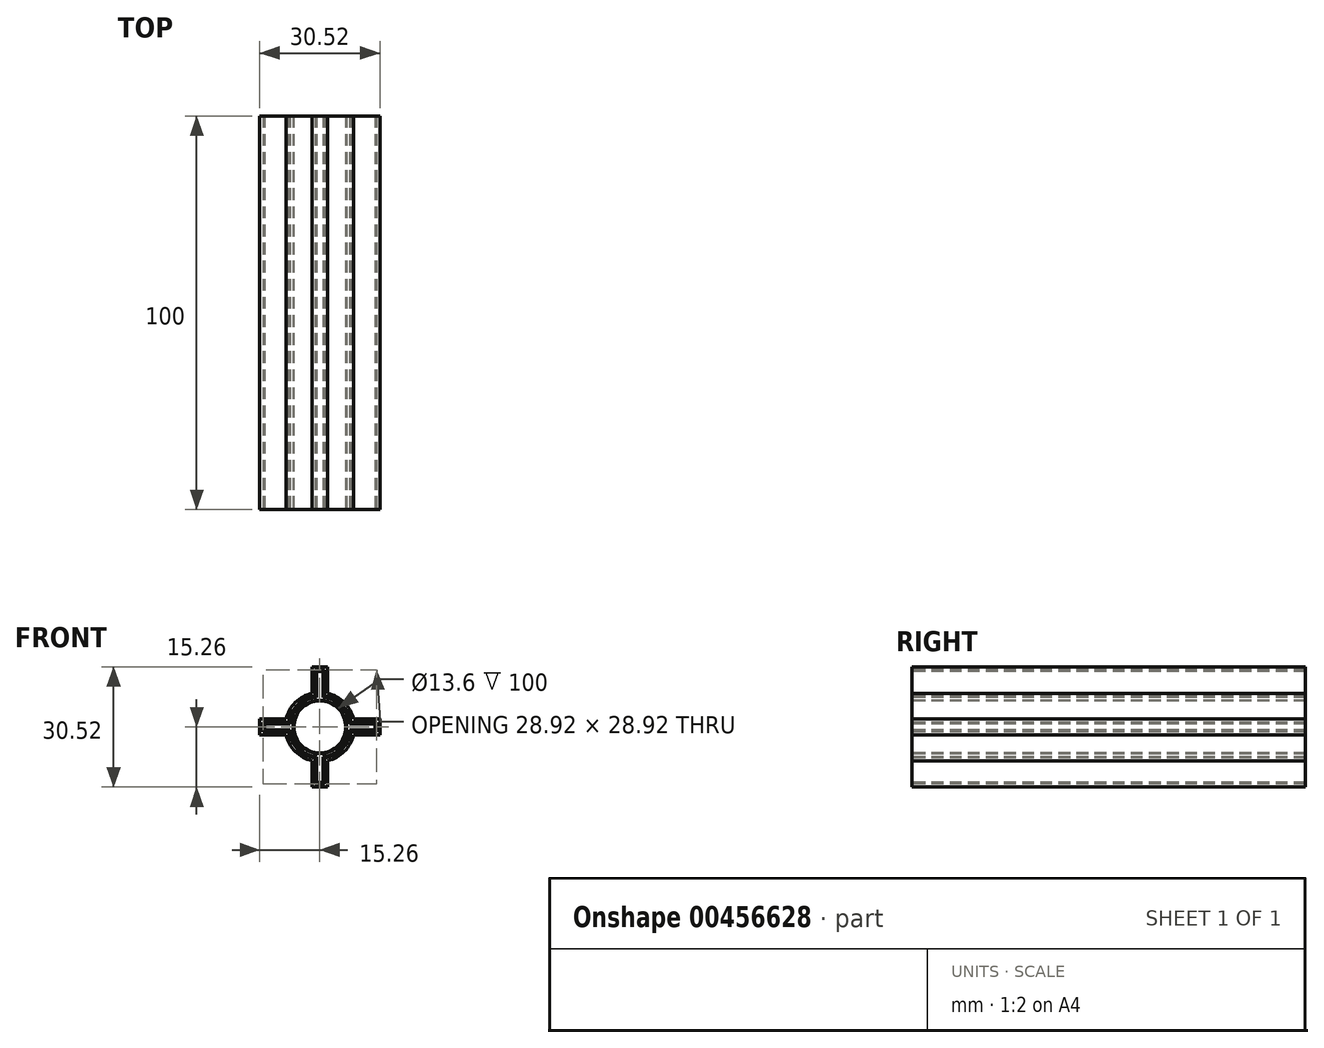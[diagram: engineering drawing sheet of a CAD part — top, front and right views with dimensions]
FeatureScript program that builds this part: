
annotation { "Feature Type Name" : "Feature", "Feature Type Description" : "" }
export const myFeature = defineFeature(function(context is Context, id is Id, definition is map)
    precondition{}
    {
        {
            var Q0;
            Q0=qCreatedBy(makeId("Front.planeOp"),FACE);
            var sketch = newSketch(context, id + "F0", { "sketchPlane" : qUnion([Q0])});
            skCircle(sketch, "E0", {"center": v(0, 0) * mm, "radius": 7.6 * mm});
            skCircle(sketch, "E1", {"center": v(0, 0) * mm, "radius": 6.6 * mm});
            skCircle(sketch, "E2", {"center": v(0, 0) * mm, "radius": 6.8 * mm});
            skLineSegment(sketch, "E3", {"start": v(-0.8, 7.56) * mm, "end": v(-0.8, 14.06) * mm});
            skLineSegment(sketch, "E4", {"start": v(-0.8, 14.06) * mm, "end": v(0.8, 14.06) * mm});
            skLineSegment(sketch, "E5", {"start": v(0.8, 14.06) * mm, "end": v(0.8, 7.56) * mm});
            skLineSegment(sketch, "E6", {"start": v(-7.56, 0.8) * mm, "end": v(-14.06, 0.8) * mm});
            skLineSegment(sketch, "E7", {"start": v(-14.06, 0.8) * mm, "end": v(-14.06, -0.8) * mm});
            skLineSegment(sketch, "E8", {"start": v(-14.06, -0.8) * mm, "end": v(-7.56, -0.8) * mm});
            skLineSegment(sketch, "E9", {"start": v(-0.8, -7.56) * mm, "end": v(-0.8, -14.06) * mm});
            skLineSegment(sketch, "E10", {"start": v(-0.8, -14.06) * mm, "end": v(0.8, -14.06) * mm});
            skLineSegment(sketch, "E11", {"start": v(0.8, -14.06) * mm, "end": v(0.8, -7.56) * mm});
            skLineSegment(sketch, "E12", {"start": v(7.56, 0.8) * mm, "end": v(14.06, 0.8) * mm});
            skLineSegment(sketch, "E13", {"start": v(14.06, 0.8) * mm, "end": v(14.06, -0.8) * mm});
            skLineSegment(sketch, "E14", {"start": v(14.06, -0.8) * mm, "end": v(7.56, -0.8) * mm});
            skPoint(sketch, "E15", {"position": v(0, -14.06) * mm});
            skPoint(sketch, "E16", {"position": v(14.06, 0) * mm});
            skPoint(sketch, "E17", {"position": v(0, 14.06) * mm});
            skPoint(sketch, "E18", {"position": v(-14.06, 0) * mm});
            skLineSegment(sketch, "E19.0", {"start": v(-14.46, -1.2) * mm, "end": v(-7.9, -1.2) * mm});
            skLineSegment(sketch, "E19.1", {"start": v(-14.46, 1.2) * mm, "end": v(-14.46, -1.2) * mm});
            skLineSegment(sketch, "E19.2", {"start": v(-7.9, 1.2) * mm, "end": v(-14.46, 1.2) * mm});
            skLineSegment(sketch, "E20.1.0", {"start": v(-1.2, -7.9) * mm, "end": v(-1.2, -14.46) * mm});
            skLineSegment(sketch, "E20.1.1", {"start": v(-1.2, -14.46) * mm, "end": v(1.2, -14.46) * mm});
            skLineSegment(sketch, "E20.1.2", {"start": v(1.2, -14.46) * mm, "end": v(1.2, -7.9) * mm});
            skLineSegment(sketch, "E20.2.0", {"start": v(7.9, -1.2) * mm, "end": v(14.46, -1.2) * mm});
            skLineSegment(sketch, "E20.2.1", {"start": v(14.46, -1.2) * mm, "end": v(14.46, 1.2) * mm});
            skLineSegment(sketch, "E20.2.2", {"start": v(14.46, 1.2) * mm, "end": v(7.9, 1.2) * mm});
            skLineSegment(sketch, "E20.3.0", {"start": v(1.2, 7.9) * mm, "end": v(1.2, 14.46) * mm});
            skLineSegment(sketch, "E20.3.1", {"start": v(1.2, 14.46) * mm, "end": v(-1.2, 14.46) * mm});
            skLineSegment(sketch, "E20.3.2", {"start": v(-1.2, 14.46) * mm, "end": v(-1.2, 7.9) * mm});
            skArc(sketch, "E21", {"start": v(-7.9, 1.2) * mm, "mid": v(-5.66, 5.66) * mm, "end": v(-1.2, 7.9) * mm});
            skArc(sketch, "E22", {"start": v(1.2, 7.9) * mm, "mid": v(5.66, 5.66) * mm, "end": v(7.9, 1.2) * mm});
            skArc(sketch, "E23", {"start": v(7.9, -1.2) * mm, "mid": v(5.66, -5.66) * mm, "end": v(1.2, -7.9) * mm});
            skArc(sketch, "E24", {"start": v(-7.9, -1.2) * mm, "mid": v(-5.66, -5.66) * mm, "end": v(-1.2, -7.9) * mm});
            skArc(sketch, "E25.0", {"start": v(-8.57, 2) * mm, "mid": v(-6.22, 6.22) * mm, "end": v(-2, 8.57) * mm});
            skLineSegment(sketch, "E25.1", {"start": v(-2, 15.26) * mm, "end": v(-2, 8.57) * mm});
            skLineSegment(sketch, "E25.2", {"start": v(2, 15.26) * mm, "end": v(-2, 15.26) * mm});
            skLineSegment(sketch, "E25.3", {"start": v(2, 8.57) * mm, "end": v(2, 15.26) * mm});
            skArc(sketch, "E25.4", {"start": v(2, 8.57) * mm, "mid": v(6.22, 6.22) * mm, "end": v(8.57, 2) * mm});
            skLineSegment(sketch, "E25.5", {"start": v(-2, -8.57) * mm, "end": v(-2, -15.26) * mm});
            skArc(sketch, "E25.6", {"start": v(-8.57, -2) * mm, "mid": v(-6.22, -6.22) * mm, "end": v(-2, -8.57) * mm});
            skLineSegment(sketch, "E25.7", {"start": v(-15.26, -2) * mm, "end": v(-8.57, -2) * mm});
            skLineSegment(sketch, "E25.8", {"start": v(-15.26, 2) * mm, "end": v(-15.26, -2) * mm});
            skLineSegment(sketch, "E25.9", {"start": v(-2, -15.26) * mm, "end": v(2, -15.26) * mm});
            skLineSegment(sketch, "E25.10", {"start": v(2, -15.26) * mm, "end": v(2, -8.57) * mm});
            skArc(sketch, "E25.11", {"start": v(8.57, -2) * mm, "mid": v(6.22, -6.22) * mm, "end": v(2, -8.57) * mm});
            skLineSegment(sketch, "E25.12", {"start": v(8.57, -2) * mm, "end": v(15.26, -2) * mm});
            skLineSegment(sketch, "E25.13", {"start": v(15.26, -2) * mm, "end": v(15.26, 2) * mm});
            skLineSegment(sketch, "E25.14", {"start": v(-8.57, 2) * mm, "end": v(-15.26, 2) * mm});
            skLineSegment(sketch, "E25.15", {"start": v(15.26, 2) * mm, "end": v(8.57, 2) * mm});
            skSolve(sketch);
        }
        {
            var Q0;
            Q0=makeQuery(id+"F0.imprint","IMPRINT",FACE,{"disambiguationData":[TD([[makeQuery(id+"F0.imprint","IMPRINT",EDGE,{"derivedFrom":sQuery(id+"F0.wireOp",EDGE,"E1")}),1.0]])]});
            extrude(context, id + "F1", {"entities" : qUnion([Q0]), "oppositeDirection" : true, "depth" : 100 * mm});
        }
        {
            var Q0;
            Q0=makeQuery(id+"F0.imprint","IMPRINT",FACE,{"disambiguationData":[TD([[makeQuery(id+"F0.imprint","IMPRINT",EDGE,{"derivedFrom":sQuery(id+"F0.wireOp",EDGE,"E2")}),-1.0]])]});
            var Q1;
            {var subQ0=sQuery(id+"F0.wireOp",EDGE,"E3");Q1=makeQuery(id+"F0.imprint","IMPRINT",FACE,{"disambiguationData":[TD([[makeQuery(id+"F0.imprint","IMPRINT",EDGE,{"derivedFrom":subQ0}),-1.0]])]});}
            var Q2;
            {var subQ0=sQuery(id+"F0.wireOp",EDGE,"E12");Q2=makeQuery(id+"F0.imprint","IMPRINT",FACE,{"disambiguationData":[TD([[makeQuery(id+"F0.imprint","IMPRINT",EDGE,{"derivedFrom":subQ0}),-1.0]])]});}
            var Q3;
            {var subQ0=sQuery(id+"F0.wireOp",EDGE,"E6");Q3=makeQuery(id+"F0.imprint","IMPRINT",FACE,{"disambiguationData":[TD([[makeQuery(id+"F0.imprint","IMPRINT",EDGE,{"derivedFrom":subQ0}),1.0]])]});}
            var Q4;
            {var subQ0=sQuery(id+"F0.wireOp",EDGE,"E9");Q4=makeQuery(id+"F0.imprint","IMPRINT",FACE,{"disambiguationData":[TD([[makeQuery(id+"F0.imprint","IMPRINT",EDGE,{"derivedFrom":subQ0}),1.0]])]});}
            extrude(context, id + "F2", {"entities" : qUnion([Q0, Q1, Q2, Q3, Q4]), "oppositeDirection" : true, "depth" : 100 * mm});
        }
        {
            var Q0;
            Q0=makeQuery(id+"F0.imprint","IMPRINT",FACE,{"disambiguationData":[TD([[makeQuery(id+"F0.imprint","IMPRINT",EDGE,{"derivedFrom":sQuery(id+"F0.wireOp",EDGE,"E19.0")}),-1.0]])]});
            extrude(context, id + "F3", {"entities" : qUnion([Q0]), "oppositeDirection" : true, "depth" : 100 * mm});
        }
    });
